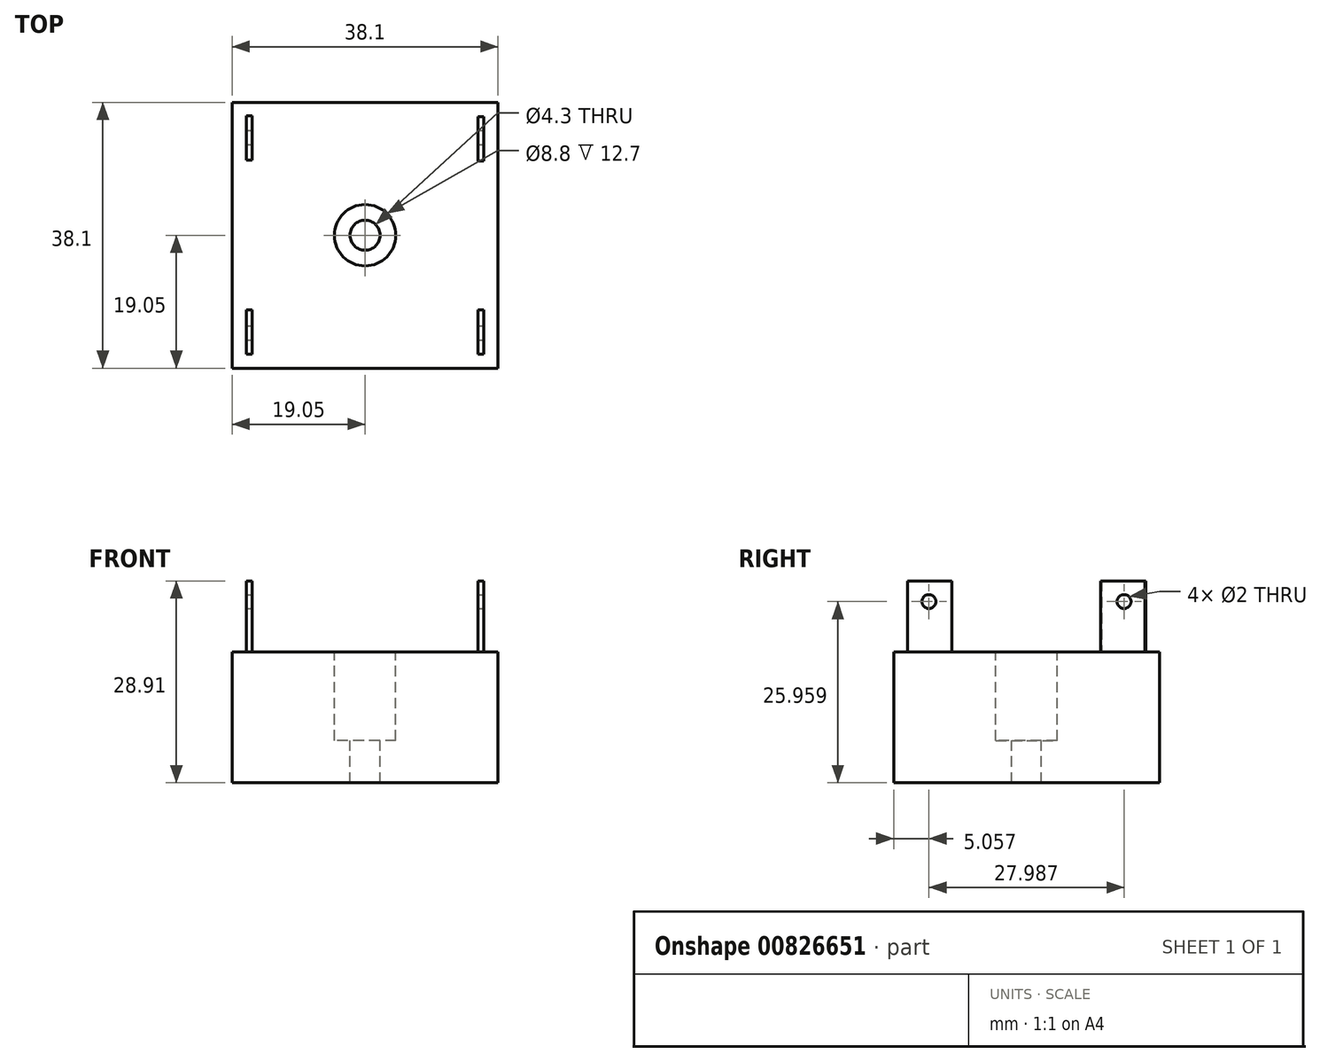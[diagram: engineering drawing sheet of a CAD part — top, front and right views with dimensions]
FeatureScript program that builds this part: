
annotation { "Feature Type Name" : "Feature", "Feature Type Description" : "" }
export const myFeature = defineFeature(function(context is Context, id is Id, definition is map)
    precondition{}
    {
        {
            var Q0;
            Q0=qCreatedBy(makeId("Top.planeOp"),FACE);
            var sketch = newSketch(context, id + "F0", { "sketchPlane" : qUnion([Q0])});
            skLineSegment(sketch, "E0.bottom", {"start": v(19.05, 19.05) * mm, "end": v(-19.05, 19.05) * mm});
            skLineSegment(sketch, "E0.top", {"start": v(19.05, -19.05) * mm, "end": v(-19.05, -19.05) * mm});
            skLineSegment(sketch, "E0.left", {"start": v(19.05, 19.05) * mm, "end": v(19.05, -19.05) * mm});
            skLineSegment(sketch, "E0.right", {"start": v(-19.05, 19.05) * mm, "end": v(-19.05, -19.05) * mm});
            skPoint(sketch, "E0.middle", {"position": v(0, 0) * mm});
            skSolve(sketch);
        }
        {
            var Q0;
            Q0 = qSketchRegion(id + "F0", true);
            extrude(context, id + "F1", {"entities" : qUnion([Q0]), "depth" : 18.75 * mm, "offsetDistance" : 25 * mm});
        }
        {
            var Q0;
            Q0=makeQuery(id+"F1.opExtrude","CAP_FACE",FACE,{"disambiguationData":[OSD([sQuery(id+"F0.wireOp",EDGE,"E0.bottom"),sQuery(id+"F0.wireOp",EDGE,"E0.top"),sQuery(id+"F0.wireOp",EDGE,"E0.left"),sQuery(id+"F0.wireOp",EDGE,"E0.right")])],"isStart":false});
            var sketch = newSketch(context, id + "F2", { "sketchPlane" : qUnion([Q0])});
            skCircle(sketch, "E1", {"center": v(0, 0) * mm, "radius": 2.15 * mm});
            skCircle(sketch, "E2", {"center": v(0, 0) * mm, "radius": 4.4 * mm});
            skSolve(sketch);
        }
        {
            var Q0;
            Q0=makeQuery(id+"F2.imprint","IMPRINT",FACE,{"disambiguationData":[TD([[makeQuery(id+"F2.imprint","IMPRINT",EDGE,{"derivedFrom":sQuery(id+"F2.wireOp",EDGE,"E1")}),1.0]])]});
            extrude(context, id + "F3", {"entities" : qUnion([Q0]), "operationType" : NewBodyOperationType.REMOVE, "oppositeDirection" : true, "depth" : 18.75 * mm, "offsetDistance" : 25 * mm});
        }
        {
            var Q0;
            Q0 = qSketchRegion(id + "F2", true);
            extrude(context, id + "F4", {"entities" : qUnion([Q0]), "operationType" : NewBodyOperationType.REMOVE, "oppositeDirection" : true, "depth" : 12.7 * mm, "offsetDistance" : 25 * mm});
        }
        {
            var Q0;
            Q0=makeQuery(id+"F2.imprint","IMPRINT",FACE,{"disambiguationData":[TD([[makeQuery(id+"F2.imprint","IMPRINT",EDGE,{"derivedFrom":sQuery(id+"F2.wireOp",EDGE,"E2")}),-1.0]])]});
            var sketch = newSketch(context, id + "F5", { "sketchPlane" : qUnion([Q0])});
            skPoint(sketch, "E3", {"position": v(17.02, -17.03) * mm});
            skPoint(sketch, "E4", {"position": v(-16.18, 16.52) * mm});
            skPoint(sketch, "E5", {"position": v(17.02, 17) * mm});
            skPoint(sketch, "E6", {"position": v(-17.02, -17.03) * mm});
            skLineSegment(sketch, "E7.bottom", {"start": v(-17.02, -17.03) * mm, "end": v(-16.2, -17.03) * mm});
            skLineSegment(sketch, "E7.top", {"start": v(-17.02, -10.68) * mm, "end": v(-16.2, -10.68) * mm});
            skLineSegment(sketch, "E7.left", {"start": v(-17.02, -17.03) * mm, "end": v(-17.02, -10.68) * mm});
            skLineSegment(sketch, "E7.right", {"start": v(-16.2, -17.03) * mm, "end": v(-16.2, -10.68) * mm});
            skLineSegment(sketch, "E8.bottom", {"start": v(17.02, -17.03) * mm, "end": v(16.2, -17.03) * mm});
            skLineSegment(sketch, "E8.top", {"start": v(17.02, -10.68) * mm, "end": v(16.2, -10.68) * mm});
            skLineSegment(sketch, "E8.left", {"start": v(17.02, -17.03) * mm, "end": v(17.02, -10.68) * mm});
            skLineSegment(sketch, "E8.right", {"start": v(16.2, -17.03) * mm, "end": v(16.2, -10.68) * mm});
            skLineSegment(sketch, "E9.bottom", {"start": v(17.02, 17) * mm, "end": v(16.2, 17) * mm});
            skLineSegment(sketch, "E9.top", {"start": v(17.02, 10.65) * mm, "end": v(16.2, 10.65) * mm});
            skLineSegment(sketch, "E9.left", {"start": v(17.02, 17) * mm, "end": v(17.02, 10.65) * mm});
            skLineSegment(sketch, "E9.right", {"start": v(16.2, 17) * mm, "end": v(16.2, 10.65) * mm});
            skLineSegment(sketch, "E10.bottom", {"start": v(-16.18, 16.52) * mm, "end": v(-15.36, 16.52) * mm});
            skLineSegment(sketch, "E10.top", {"start": v(-16.18, 10.17) * mm, "end": v(-15.36, 10.17) * mm});
            skLineSegment(sketch, "E10.left", {"start": v(-16.18, 16.52) * mm, "end": v(-16.18, 10.17) * mm});
            skLineSegment(sketch, "E10.right", {"start": v(-15.36, 16.52) * mm, "end": v(-15.36, 10.17) * mm});
            skSolve(sketch);
        }
        {
            var Q0;
            Q0 = qSketchRegion(id + "F5", true);
            extrude(context, id + "F6", {"entities" : qUnion([Q0]), "depth" : 10.16 * mm, "offsetDistance" : 25 * mm});
        }
        {
            var Q0;
            Q0=makeQuery(id+"F6.opExtrude","SWEPT_BODY",BODY,{"disambiguationData":[OSD([sQuery(id+"F5.wireOp",EDGE,"E10.bottom"),sQuery(id+"F5.wireOp",EDGE,"E10.top"),sQuery(id+"F5.wireOp",EDGE,"E10.left"),sQuery(id+"F5.wireOp",EDGE,"E10.right")])]});
            transform(context, id + "F7", {"entities" : qUnion([Q0]), "transformType" : TransformType.TRANSLATION_3D, "dx" : -0.83 * mm, "dy" : 0.58 * mm, "dz" : 0 * mm, "makeCopy" : false});
        }
        {
            var Q0;
            Q0=makeQuery(id+"F6.opExtrude","SWEPT_EDGE",EDGE,{"disambiguationData":[OSD([sQuery(id+"F5.wireOp",EDGE,"E9.bottom"),sQuery(id+"F5.wireOp",EDGE,"E9.left")])]});
            cPoint(context, id + "F8", {"entities" : qUnion([Q0]), "parameter" : 0.5});
        }
        {
            var Q0;
            Q0 = qCreatedBy(id + "F8" ,VERTEX);
            var Q1;
            Q1=makeQuery(id+"F6.opExtrude","SWEPT_FACE",FACE,{"disambiguationData":[OSD([sQuery(id+"F5.wireOp",EDGE,"E8.left")])]});
            cPlane(context, id + "F9", {"entities" : qUnion([Q0, Q1]), "cplaneType" : CPlaneType.PLANE_POINT, "offset" : 25 * mm, "width" : 150 * mm, "height" : 150 * mm});
        }
        {
            var Q0;
            Q0=qCreatedBy(id+"F9.planeOp",FACE);
            var sketch = newSketch(context, id + "F10", { "sketchPlane" : qUnion([Q0])});
            skCircle(sketch, "E11", {"center": v(-14, 25.96) * mm, "radius": 1 * mm});
            skCircle(sketch, "E12.MirrorC", {"center": v(14, 25.96) * mm, "radius": 1 * mm});
            skSolve(sketch);
        }
        {
            var Q0;
            Q0 = qSketchRegion(id + "F10", true);
            extrude(context, id + "F11", {"entities" : qUnion([Q0]), "operationType" : NewBodyOperationType.REMOVE, "oppositeDirection" : true, "depth" : 40 * mm, "offsetDistance" : 25 * mm});
        }
    });
